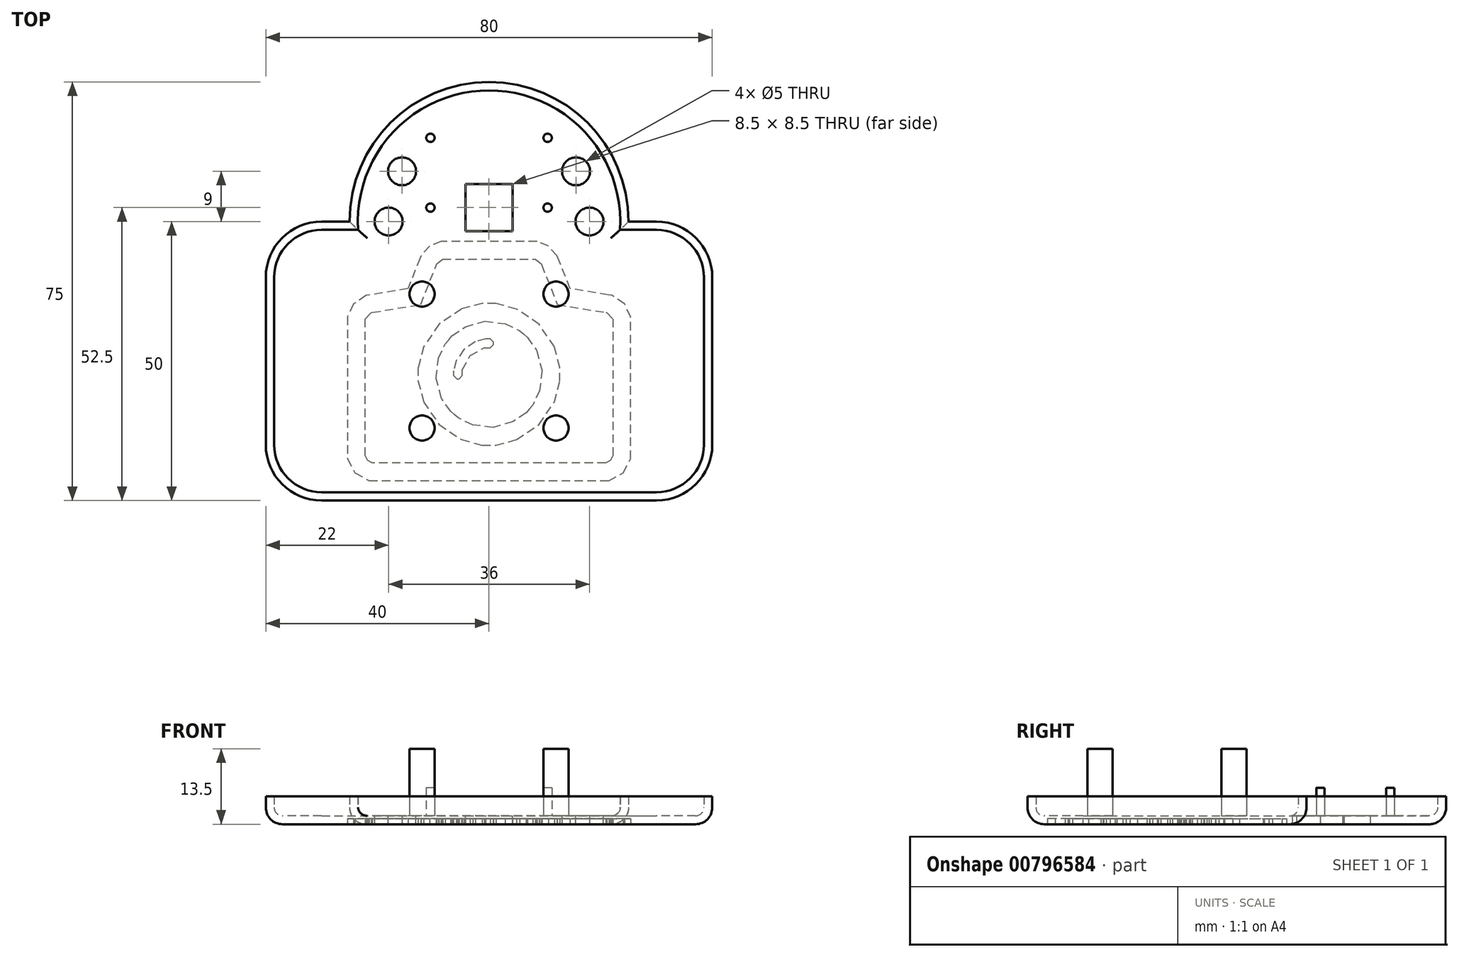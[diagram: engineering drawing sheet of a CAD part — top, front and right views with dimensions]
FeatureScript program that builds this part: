
annotation { "Feature Type Name" : "Feature", "Feature Type Description" : "" }
export const myFeature = defineFeature(function(context is Context, id is Id, definition is map)
    precondition{}
    {
        {
            var Q0;
            Q0=qCreatedBy(makeId("Top.planeOp"),FACE);
            var sketch = newSketch(context, id + "F0", { "sketchPlane" : qUnion([Q0])});
            skLineSegment(sketch, "E0.bottom", {"start": v(12.5, -12) * mm, "end": v(-12.5, -12) * mm});
            skLineSegment(sketch, "E0.top", {"start": v(12.5, 12) * mm, "end": v(-12.5, 12) * mm});
            skLineSegment(sketch, "E0.left", {"start": v(12.5, -12) * mm, "end": v(12.5, 12) * mm});
            skLineSegment(sketch, "E0.right", {"start": v(-12.5, -12) * mm, "end": v(-12.5, 12) * mm});
            skPoint(sketch, "E0.middle", {"position": v(0, 0) * mm});
            skPoint(sketch, "E1", {"position": v(-10.5, 10) * mm});
            skCircle(sketch, "E2", {"center": v(-10.5, 10) * mm, "radius": 0.75 * mm});
            skCircle(sketch, "E3.1.0.0", {"center": v(10.5, 10) * mm, "radius": 0.75 * mm});
            skLineSegment(sketch, "E3.direction1", {"start": v(-10.5, 10) * mm, "end": v(10.5, 10) * mm, "construction": true});
            skCircle(sketch, "E4.0.1.0", {"center": v(-10.5, -2.5) * mm, "radius": 0.75 * mm});
            skCircle(sketch, "E4.0.1.1", {"center": v(10.5, -2.5) * mm, "radius": 0.75 * mm});
            skLineSegment(sketch, "E4.direction1", {"start": v(-10.5, 10) * mm, "end": v(14.5, 10) * mm, "construction": true});
            skLineSegment(sketch, "E4.direction2", {"start": v(-10.5, 10) * mm, "end": v(-10.5, -2.5) * mm, "construction": true});
            skLineSegment(sketch, "E5.bottom", {"start": v(30, 25) * mm, "end": v(-30, 25) * mm});
            skLineSegment(sketch, "E5.top", {"start": v(30, -25) * mm, "end": v(-30, -25) * mm});
            skLineSegment(sketch, "E5.left", {"start": v(40, 15) * mm, "end": v(40, -15) * mm});
            skLineSegment(sketch, "E5.right", {"start": v(-40, 15) * mm, "end": v(-40, -15) * mm});
            skPoint(sketch, "E6.visualSharp", {"position": v(-40, 25) * mm});
            skArc(sketch, "E6.filletArc", {"start": v(-30, 25) * mm, "mid": v(-37.07, 22.07) * mm, "end": v(-40, 15) * mm});
            skPoint(sketch, "E7.visualSharp", {"position": v(40, 25) * mm});
            skArc(sketch, "E7.filletArc", {"start": v(40, 15) * mm, "mid": v(37.07, 22.07) * mm, "end": v(30, 25) * mm});
            skPoint(sketch, "E8.visualSharp", {"position": v(40, -25) * mm});
            skArc(sketch, "E8.filletArc", {"start": v(30, -25) * mm, "mid": v(37.07, -22.07) * mm, "end": v(40, -15) * mm});
            skPoint(sketch, "E9.visualSharp", {"position": v(-40, -25) * mm});
            skArc(sketch, "E9.filletArc", {"start": v(-40, -15) * mm, "mid": v(-37.07, -22.07) * mm, "end": v(-30, -25) * mm});
            skCircle(sketch, "E10", {"center": v(0, 25) * mm, "radius": 25 * mm});
            skSolve(sketch);
        }
        {
            var Q0;
            Q0=makeQuery(id+"F0.imprint","IMPRINT",FACE,{"disambiguationData":[TD([[makeQuery(id+"F0.imprint","IMPRINT",EDGE,{"derivedFrom":sQuery(id+"F0.wireOp",EDGE,"E0.bottom")}),1.0]])]});
            var Q1;
            Q1=makeQuery(id+"F0.imprint","IMPRINT",FACE,{"disambiguationData":[TD([[makeQuery(id+"F0.imprint","IMPRINT",EDGE,{"derivedFrom":sQuery(id+"F0.wireOp",EDGE,"E2")}),1.0]])]});
            var Q2;
            Q2=makeQuery(id+"F0.imprint","IMPRINT",FACE,{"disambiguationData":[TD([[makeQuery(id+"F0.imprint","IMPRINT",EDGE,{"derivedFrom":sQuery(id+"F0.wireOp",EDGE,"E3.1.0.0")}),1.0]])]});
            var Q3;
            Q3=makeQuery(id+"F0.imprint","IMPRINT",FACE,{"disambiguationData":[TD([[makeQuery(id+"F0.imprint","IMPRINT",EDGE,{"derivedFrom":sQuery(id+"F0.wireOp",EDGE,"E4.0.1.0")}),1.0]])]});
            var Q4;
            Q4=makeQuery(id+"F0.imprint","IMPRINT",FACE,{"disambiguationData":[TD([[makeQuery(id+"F0.imprint","IMPRINT",EDGE,{"derivedFrom":sQuery(id+"F0.wireOp",EDGE,"E4.0.1.1")}),1.0]])]});
            var Q5;
            Q5=makeQuery(id+"F0.imprint","IMPRINT",FACE,{"disambiguationData":[TD([[makeQuery(id+"F0.imprint","IMPRINT",EDGE,{"derivedFrom":sQuery(id+"F0.wireOp",EDGE,"E0.bottom")}),-1.0]])]});
            var Q6;
            {var subQ0=sQuery(id+"F0.wireOp",EDGE,"E10");var subQ1=sQuery(id+"F0.wireOp",EDGE,"E0.top");var subQ2=makeQuery(id+"F0.imprint","INTERSECT",VERTEX,{"disambiguationData":[OD(0.0)],"derivedFrom":[subQ1,subQ0]});Q6=makeQuery(id+"F0.imprint","IMPRINT",FACE,{"disambiguationData":[TD([[makeQuery(id+"F0.imprint","IMPRINT",EDGE,{"disambiguationData":[TD([[subQ2,-1.0]])],"derivedFrom":subQ1}),1.0]])]});}
            var Q7;
            {var subQ0=sQuery(id+"F0.wireOp",EDGE,"E10");var subQ1=sQuery(id+"F0.wireOp",EDGE,"E0.top");var subQ2=makeQuery(id+"F0.imprint","INTERSECT",VERTEX,{"disambiguationData":[OD(0.0)],"derivedFrom":[subQ1,subQ0]});Q7=makeQuery(id+"F0.imprint","IMPRINT",FACE,{"disambiguationData":[TD([[makeQuery(id+"F0.imprint","IMPRINT",EDGE,{"disambiguationData":[TD([[subQ2,-1.0]])],"derivedFrom":subQ1}),-1.0]])]});}
            var Q8;
            {var subQ0=sQuery(id+"F0.wireOp",EDGE,"E10");var subQ1=sQuery(id+"F0.wireOp",EDGE,"E5.bottom");var subQ2=makeQuery(id+"F0.imprint","INTERSECT",VERTEX,{"disambiguationData":[OD(0.0)],"derivedFrom":[subQ1,subQ0]});Q8=makeQuery(id+"F0.imprint","IMPRINT",FACE,{"disambiguationData":[TD([[makeQuery(id+"F0.imprint","IMPRINT",EDGE,{"disambiguationData":[TD([[subQ2,-1.0]])],"derivedFrom":subQ1}),-1.0]])]});}
            extrude(context, id + "F1", {"entities" : qUnion([Q0, Q1, Q2, Q3, Q4, Q5, Q6, Q7, Q8]), "depth" : 5 * mm, "offsetDistance" : 25 * mm});
        }
        {
            var Q0;
            Q0=makeQuery(id+"F1.opExtrude","CAP_EDGE",EDGE,{"disambiguationData":[OSD([sQuery(id+"F0.wireOp",EDGE,"E10")])],"isStart":true});
            var Q1;
            Q1=makeQuery(id+"F1.opExtrude","CAP_EDGE",EDGE,{"disambiguationData":[OSD([sQuery(id+"F0.wireOp",EDGE,"E5.right")])],"isStart":true});
            fillet(context, id + "F2", {"entities" : qUnion([Q0, Q1]), "radius" : 3 * mm, "tangentPropagation" : true, "allowEdgeOverflow" : false});
        }
        {
            var Q0;
            Q0=makeQuery(id+"F1.opExtrude","CAP_FACE",FACE,{"disambiguationData":[OSD([sQuery(id+"F0.wireOp",EDGE,"E5.bottom"),sQuery(id+"F0.wireOp",EDGE,"E5.top"),sQuery(id+"F0.wireOp",EDGE,"E5.left"),sQuery(id+"F0.wireOp",EDGE,"E5.right"),sQuery(id+"F0.wireOp",EDGE,"E6.filletArc"),sQuery(id+"F0.wireOp",EDGE,"E7.filletArc"),sQuery(id+"F0.wireOp",EDGE,"E8.filletArc"),sQuery(id+"F0.wireOp",EDGE,"E9.filletArc")])],"isStart":false});
            shell(context, id + "F3", {"entities" : qUnion([Q0]), "thickness" : 1.5 * mm});
        }
        {
            var Q0;
            Q0=makeQuery(id+"F3.opShell","OFFSET_FACE",FACE,{"disambiguationData":[OSD([sQuery(id+"F0.wireOp",EDGE,"E5.bottom"),sQuery(id+"F0.wireOp",EDGE,"E5.top"),sQuery(id+"F0.wireOp",EDGE,"E5.left"),sQuery(id+"F0.wireOp",EDGE,"E5.right"),sQuery(id+"F0.wireOp",EDGE,"E6.filletArc"),sQuery(id+"F0.wireOp",EDGE,"E7.filletArc"),sQuery(id+"F0.wireOp",EDGE,"E8.filletArc"),sQuery(id+"F0.wireOp",EDGE,"E9.filletArc")])]});
            var sketch = newSketch(context, id + "F4", { "sketchPlane" : qUnion([Q0])});
            skCircle(sketch, "E11", {"center": v(-12, 12) * mm, "radius": 2.25 * mm});
            skCircle(sketch, "E12.1.0", {"center": v(-12, -12) * mm, "radius": 2.25 * mm});
            skCircle(sketch, "E12.2.0", {"center": v(12, -12) * mm, "radius": 2.25 * mm});
            skCircle(sketch, "E12.3.0", {"center": v(12, 12) * mm, "radius": 2.25 * mm});
            skPoint(sketch, "E12.center", {"position": v(0, 0) * mm});
            skSolve(sketch);
        }
        {
            var Q0;
            Q0=makeQuery(id+"F4.imprint","IMPRINT",FACE,{"disambiguationData":[TD([[makeQuery(id+"F4.imprint","IMPRINT",EDGE,{"derivedFrom":sQuery(id+"F4.wireOp",EDGE,"E11")}),1.0]])]});
            var Q1;
            Q1=makeQuery(id+"F4.imprint","IMPRINT",FACE,{"disambiguationData":[TD([[makeQuery(id+"F4.imprint","IMPRINT",EDGE,{"derivedFrom":sQuery(id+"F4.wireOp",EDGE,"E12.3.0")}),1.0]])]});
            var Q2;
            Q2=makeQuery(id+"F4.imprint","IMPRINT",FACE,{"disambiguationData":[TD([[makeQuery(id+"F4.imprint","IMPRINT",EDGE,{"derivedFrom":sQuery(id+"F4.wireOp",EDGE,"E12.1.0")}),1.0]])]});
            var Q3;
            Q3=makeQuery(id+"F4.imprint","IMPRINT",FACE,{"disambiguationData":[TD([[makeQuery(id+"F4.imprint","IMPRINT",EDGE,{"derivedFrom":sQuery(id+"F4.wireOp",EDGE,"E12.2.0")}),1.0]])]});
            extrude(context, id + "F5", {"entities" : qUnion([Q0, Q1, Q2, Q3]), "operationType" : NewBodyOperationType.ADD, "depth" : 12 * mm, "offsetDistance" : 25 * mm});
        }
        {
            var Q0;
            Q0=makeQuery(id+"F3.opShell","OFFSET_FACE",FACE,{"disambiguationData":[OSD([sQuery(id+"F0.wireOp",EDGE,"E5.bottom"),sQuery(id+"F0.wireOp",EDGE,"E5.top"),sQuery(id+"F0.wireOp",EDGE,"E5.left"),sQuery(id+"F0.wireOp",EDGE,"E5.right"),sQuery(id+"F0.wireOp",EDGE,"E6.filletArc"),sQuery(id+"F0.wireOp",EDGE,"E7.filletArc"),sQuery(id+"F0.wireOp",EDGE,"E8.filletArc"),sQuery(id+"F0.wireOp",EDGE,"E9.filletArc"),sQuery(id+"F0.wireOp",EDGE,"E10")])]});
            var sketch = newSketch(context, id + "F6", { "sketchPlane" : qUnion([Q0])});
            skLineSegment(sketch, "E13.bottom", {"start": v(12.5, 18) * mm, "end": v(-12.5, 18) * mm});
            skLineSegment(sketch, "E13.top", {"start": v(12.5, 42) * mm, "end": v(-12.5, 42) * mm});
            skLineSegment(sketch, "E13.left", {"start": v(12.5, 18) * mm, "end": v(12.5, 42) * mm});
            skLineSegment(sketch, "E13.right", {"start": v(-12.5, 18) * mm, "end": v(-12.5, 42) * mm});
            skPoint(sketch, "E13.middle", {"position": v(0, 30) * mm});
            skPoint(sketch, "E14", {"position": v(-10.5, 40) * mm});
            skCircle(sketch, "E15", {"center": v(-10.5, 40) * mm, "radius": 0.75 * mm});
            skCircle(sketch, "E16.1.0.0", {"center": v(10.5, 40) * mm, "radius": 0.75 * mm});
            skLineSegment(sketch, "E16.direction1", {"start": v(-10.5, 40) * mm, "end": v(10.5, 40) * mm, "construction": true});
            skCircle(sketch, "E17.0.1.0", {"center": v(-10.5, 27.5) * mm, "radius": 0.75 * mm});
            skCircle(sketch, "E17.0.1.1", {"center": v(10.5, 27.5) * mm, "radius": 0.75 * mm});
            skLineSegment(sketch, "E17.direction1", {"start": v(-10.5, 40) * mm, "end": v(14.5, 40) * mm, "construction": true});
            skLineSegment(sketch, "E17.direction2", {"start": v(-10.5, 40) * mm, "end": v(-10.5, 27.5) * mm, "construction": true});
            skLineSegment(sketch, "E18.bottom", {"start": v(-4.25, 31.75) * mm, "end": v(4.25, 31.75) * mm});
            skLineSegment(sketch, "E18.top", {"start": v(-4.25, 23.25) * mm, "end": v(4.25, 23.25) * mm});
            skLineSegment(sketch, "E18.left", {"start": v(-4.25, 31.75) * mm, "end": v(-4.25, 23.25) * mm});
            skLineSegment(sketch, "E18.right", {"start": v(4.25, 31.75) * mm, "end": v(4.25, 23.25) * mm});
            skSolve(sketch);
        }
        {
            var Q0;
            Q0=makeQuery(id+"F6.imprint","IMPRINT",FACE,{"disambiguationData":[TD([[makeQuery(id+"F6.imprint","IMPRINT",EDGE,{"derivedFrom":sQuery(id+"F6.wireOp",EDGE,"E15")}),1.0]])]});
            var Q1;
            Q1=makeQuery(id+"F6.imprint","IMPRINT",FACE,{"disambiguationData":[TD([[makeQuery(id+"F6.imprint","IMPRINT",EDGE,{"derivedFrom":sQuery(id+"F6.wireOp",EDGE,"E16.1.0.0")}),1.0]])]});
            var Q2;
            Q2=makeQuery(id+"F6.imprint","IMPRINT",FACE,{"disambiguationData":[TD([[makeQuery(id+"F6.imprint","IMPRINT",EDGE,{"derivedFrom":sQuery(id+"F6.wireOp",EDGE,"E17.0.1.0")}),1.0]])]});
            var Q3;
            Q3=makeQuery(id+"F6.imprint","IMPRINT",FACE,{"disambiguationData":[TD([[makeQuery(id+"F6.imprint","IMPRINT",EDGE,{"derivedFrom":sQuery(id+"F6.wireOp",EDGE,"E17.0.1.1")}),1.0]])]});
            extrude(context, id + "F7", {"entities" : qUnion([Q0, Q1, Q2, Q3]), "operationType" : NewBodyOperationType.ADD, "depth" : 5 * mm, "offsetDistance" : 25 * mm});
        }
        {
            var Q0;
            Q0=makeQuery(id+"F6.imprint","IMPRINT",FACE,{"disambiguationData":[TD([[makeQuery(id+"F6.imprint","IMPRINT",EDGE,{"derivedFrom":sQuery(id+"F6.wireOp",EDGE,"E18.bottom")}),-1.0]])]});
            extrude(context, id + "F8", {"entities" : qUnion([Q0]), "operationType" : NewBodyOperationType.REMOVE, "oppositeDirection" : true, "depth" : 25 * mm, "offsetDistance" : 25 * mm});
        }
        {
            var Q0;
            Q0=makeQuery(id+"F6.imprint","IMPRINT",FACE,{"disambiguationData":[TD([[makeQuery(id+"F6.imprint","IMPRINT",EDGE,{"derivedFrom":sQuery(id+"F6.wireOp",EDGE,"E13.bottom")}),1.0]])]});
            var sketch = newSketch(context, id + "F9", { "sketchPlane" : qUnion([Q0])});
            skPoint(sketch, "E19", {"position": v(0, 43) * mm});
            skPoint(sketch, "E20", {"position": v(0, 25) * mm});
            skPoint(sketch, "E21.1.0", {"position": v(-9, 40.59) * mm});
            skPoint(sketch, "E21.2.0", {"position": v(-15.59, 34) * mm});
            skPoint(sketch, "E21.3.0", {"position": v(-18, 25) * mm});
            skPoint(sketch, "E21.4.0", {"position": v(-15.59, 16) * mm});
            skPoint(sketch, "E21.5.0", {"position": v(-9, 9.41) * mm});
            skPoint(sketch, "E21.6.0", {"position": v(0, 7) * mm});
            skPoint(sketch, "E21.7.0", {"position": v(9, 9.41) * mm});
            skPoint(sketch, "E21.8.0", {"position": v(15.59, 16) * mm});
            skPoint(sketch, "E21.9.0", {"position": v(18, 25) * mm});
            skPoint(sketch, "E21.10.0", {"position": v(15.59, 34) * mm});
            skPoint(sketch, "E21.11.0", {"position": v(9, 40.59) * mm});
            skSolve(sketch);
        }
        {
            var Q0;
            Q0=sQuery(id+"F9.wireOp",VERTEX,"E21.2.0");
            var Q1;
            Q1=sQuery(id+"F9.wireOp",VERTEX,"E21.3.0");
            var Q2;
            Q2=sQuery(id+"F9.wireOp",VERTEX,"E21.10.0");
            var Q3;
            Q3=sQuery(id+"F9.wireOp",VERTEX,"E21.9.0");
            var Q4;
            Q4=makeQuery(id+"F1.opExtrude","SWEPT_BODY",BODY,{"disambiguationData":[OSD([sQuery(id+"F0.wireOp",EDGE,"E5.bottom"),sQuery(id+"F0.wireOp",EDGE,"E5.top"),sQuery(id+"F0.wireOp",EDGE,"E5.left"),sQuery(id+"F0.wireOp",EDGE,"E5.right"),sQuery(id+"F0.wireOp",EDGE,"E6.filletArc"),sQuery(id+"F0.wireOp",EDGE,"E7.filletArc"),sQuery(id+"F0.wireOp",EDGE,"E8.filletArc"),sQuery(id+"F0.wireOp",EDGE,"E9.filletArc"),sQuery(id+"F0.wireOp",EDGE,"E10")])]});
            hole(context, id + "F10", {"style" : HoleStyle.SIMPLE, "endStyle" : HoleEndStyle.THROUGH, "holeDiameter" : 5 * mm, "majorDiameter" : 5 * mm, "isTappedThrough" : true, "tappedDepth" : 12 * mm, "tapClearance" : 3, "locations" : qUnion([Q0, Q1, Q2, Q3]), "scope" : qUnion([Q4])});
        }
        {
            var Q0;
            Q0=qCreatedBy(makeId("Top.planeOp"),FACE);
            var sketch = newSketch(context, id + "F11", { "sketchPlane" : qUnion([Q0])});
            skLineSegment(sketch, "E22", {"start": v(0, 20.64) * mm, "end": v(-2.48, 20.64) * mm});
            skLineSegment(sketch, "E23", {"start": v(-2.48, 20.64) * mm, "end": v(-9.89, 18.65) * mm});
            skLineSegment(sketch, "E24", {"start": v(-9.89, 18.65) * mm, "end": v(-17.96, 13.2) * mm});
            skLineSegment(sketch, "E25", {"start": v(-17.96, 13.2) * mm, "end": v(-23.42, 5.13) * mm});
            skLineSegment(sketch, "E26", {"start": v(-23.42, 5.13) * mm, "end": v(-25.4, -2.28) * mm});
            skLineSegment(sketch, "E27", {"start": v(-25.4, -2.28) * mm, "end": v(-25.4, -4.76) * mm});
            skLineSegment(sketch, "E28", {"start": v(-25.4, -4.76) * mm, "end": v(-25.4, -7.23) * mm});
            skLineSegment(sketch, "E29", {"start": v(-25.4, -7.23) * mm, "end": v(-23.42, -14.63) * mm});
            skLineSegment(sketch, "E30", {"start": v(-23.42, -14.63) * mm, "end": v(-17.96, -22.72) * mm});
            skLineSegment(sketch, "E31", {"start": v(-17.96, -22.72) * mm, "end": v(-9.89, -28.16) * mm});
            skLineSegment(sketch, "E32", {"start": v(-9.89, -28.16) * mm, "end": v(-2.48, -30.16) * mm});
            skLineSegment(sketch, "E33", {"start": v(-2.48, -30.16) * mm, "end": v(0, -30.16) * mm});
            skLineSegment(sketch, "E34", {"start": v(0, -30.16) * mm, "end": v(2.46, -30.16) * mm});
            skLineSegment(sketch, "E35", {"start": v(2.46, -30.16) * mm, "end": v(9.87, -28.16) * mm});
            skLineSegment(sketch, "E36", {"start": v(9.87, -28.16) * mm, "end": v(17.96, -22.72) * mm});
            skLineSegment(sketch, "E37", {"start": v(17.96, -22.72) * mm, "end": v(23.4, -14.63) * mm});
            skLineSegment(sketch, "E38", {"start": v(23.4, -14.63) * mm, "end": v(25.4, -7.23) * mm});
            skLineSegment(sketch, "E39", {"start": v(25.4, -7.23) * mm, "end": v(25.4, -4.76) * mm});
            skLineSegment(sketch, "E40", {"start": v(25.4, -4.76) * mm, "end": v(25.4, -2.28) * mm});
            skLineSegment(sketch, "E41", {"start": v(25.4, -2.28) * mm, "end": v(23.4, 5.13) * mm});
            skLineSegment(sketch, "E42", {"start": v(23.4, 5.13) * mm, "end": v(17.96, 13.2) * mm});
            skLineSegment(sketch, "E43", {"start": v(17.96, 13.2) * mm, "end": v(9.87, 18.65) * mm});
            skLineSegment(sketch, "E44", {"start": v(9.87, 18.65) * mm, "end": v(2.46, 20.64) * mm});
            skLineSegment(sketch, "E45", {"start": v(2.46, 20.64) * mm, "end": v(0, 20.64) * mm});
            skLineSegment(sketch, "E46", {"start": v(14.47, -17.16) * mm, "end": v(13.26, -18.57) * mm});
            skLineSegment(sketch, "E47", {"start": v(13.26, -18.57) * mm, "end": v(8.5, -21.81) * mm});
            skLineSegment(sketch, "E48", {"start": v(8.5, -21.81) * mm, "end": v(1.46, -23.75) * mm});
            skLineSegment(sketch, "E49", {"start": v(1.46, -23.75) * mm, "end": v(-5.8, -22.92) * mm});
            skLineSegment(sketch, "E50", {"start": v(-5.8, -22.92) * mm, "end": v(-11, -20.42) * mm});
            skLineSegment(sketch, "E51", {"start": v(-11, -20.42) * mm, "end": v(-12.4, -19.23) * mm});
            skLineSegment(sketch, "E52", {"start": v(-12.4, -19.23) * mm, "end": v(-13.8, -18.02) * mm});
            skLineSegment(sketch, "E53", {"start": v(-13.8, -18.02) * mm, "end": v(-17.07, -13.26) * mm});
            skLineSegment(sketch, "E54", {"start": v(-17.07, -13.26) * mm, "end": v(-19, -6.22) * mm});
            skLineSegment(sketch, "E55", {"start": v(-19, -6.22) * mm, "end": v(-18.16, 1.03) * mm});
            skLineSegment(sketch, "E56", {"start": v(-18.16, 1.03) * mm, "end": v(-15.66, 6.22) * mm});
            skLineSegment(sketch, "E57", {"start": v(-15.66, 6.22) * mm, "end": v(-14.45, 7.62) * mm});
            skLineSegment(sketch, "E58", {"start": v(-14.45, 7.62) * mm, "end": v(-13.26, 9.03) * mm});
            skLineSegment(sketch, "E59", {"start": v(-13.26, 9.03) * mm, "end": v(-8.5, 12.29) * mm});
            skLineSegment(sketch, "E60", {"start": v(-8.5, 12.29) * mm, "end": v(-1.47, 14.24) * mm});
            skLineSegment(sketch, "E61", {"start": v(-1.47, 14.24) * mm, "end": v(5.79, 13.4) * mm});
            skLineSegment(sketch, "E62", {"start": v(5.79, 13.4) * mm, "end": v(10.98, 10.9) * mm});
            skLineSegment(sketch, "E63", {"start": v(10.98, 10.9) * mm, "end": v(12.4, 9.7) * mm});
            skLineSegment(sketch, "E64", {"start": v(12.4, 9.7) * mm, "end": v(13.8, 8.5) * mm});
            skLineSegment(sketch, "E65", {"start": v(13.8, 8.5) * mm, "end": v(17.05, 3.74) * mm});
            skLineSegment(sketch, "E66", {"start": v(17.05, 3.74) * mm, "end": v(18.98, -3.3) * mm});
            skLineSegment(sketch, "E67", {"start": v(18.98, -3.3) * mm, "end": v(18.16, -10.55) * mm});
            skLineSegment(sketch, "E68", {"start": v(18.16, -10.55) * mm, "end": v(15.68, -15.76) * mm});
            skLineSegment(sketch, "E69", {"start": v(15.68, -15.76) * mm, "end": v(14.47, -17.16) * mm});
            skLineSegment(sketch, "E70", {"start": v(0, 7.94) * mm, "end": v(-1.24, 7.94) * mm});
            skLineSegment(sketch, "E71", {"start": v(-1.24, 7.94) * mm, "end": v(-4.94, 6.95) * mm});
            skLineSegment(sketch, "E72", {"start": v(-4.94, 6.95) * mm, "end": v(-8.98, 4.22) * mm});
            skLineSegment(sketch, "E73", {"start": v(-8.98, 4.22) * mm, "end": v(-11.7, 0.18) * mm});
            skLineSegment(sketch, "E74", {"start": v(-11.7, 0.18) * mm, "end": v(-12.7, -3.52) * mm});
            skLineSegment(sketch, "E75", {"start": v(-12.7, -3.52) * mm, "end": v(-12.7, -4.76) * mm});
            skLineSegment(sketch, "E76", {"start": v(-12.7, -4.76) * mm, "end": v(-12.7, -5.16) * mm});
            skLineSegment(sketch, "E77", {"start": v(-12.7, -5.16) * mm, "end": v(-11.5, -6.35) * mm});
            skLineSegment(sketch, "E78", {"start": v(-11.5, -6.35) * mm, "end": v(-11.11, -6.35) * mm});
            skLineSegment(sketch, "E79", {"start": v(-11.11, -6.35) * mm, "end": v(-10.72, -6.35) * mm});
            skLineSegment(sketch, "E80", {"start": v(-10.72, -6.35) * mm, "end": v(-9.52, -5.16) * mm});
            skLineSegment(sketch, "E81", {"start": v(-9.52, -5.16) * mm, "end": v(-9.52, -4.76) * mm});
            skLineSegment(sketch, "E82", {"start": v(-9.52, -4.76) * mm, "end": v(-9.52, -3.08) * mm});
            skLineSegment(sketch, "E83", {"start": v(-9.52, -3.08) * mm, "end": v(-6.75, 1.98) * mm});
            skLineSegment(sketch, "E84", {"start": v(-6.75, 1.98) * mm, "end": v(-1.69, 4.76) * mm});
            skLineSegment(sketch, "E85", {"start": v(-1.69, 4.76) * mm, "end": v(0, 4.76) * mm});
            skLineSegment(sketch, "E86", {"start": v(0, 4.76) * mm, "end": v(0.4, 4.76) * mm});
            skLineSegment(sketch, "E87", {"start": v(0.4, 4.76) * mm, "end": v(1.59, 5.95) * mm});
            skLineSegment(sketch, "E88", {"start": v(1.59, 5.95) * mm, "end": v(1.59, 6.35) * mm});
            skLineSegment(sketch, "E89", {"start": v(1.59, 6.35) * mm, "end": v(1.59, 6.75) * mm});
            skLineSegment(sketch, "E90", {"start": v(1.59, 6.75) * mm, "end": v(0.4, 7.94) * mm});
            skLineSegment(sketch, "E91", {"start": v(0.4, 7.94) * mm, "end": v(0, 7.94) * mm});
            skLineSegment(sketch, "E92", {"start": v(42.83, 23.68) * mm, "end": v(29.07, 25.98) * mm});
            skLineSegment(sketch, "E93", {"start": v(29.07, 25.98) * mm, "end": v(24.72, 36.88) * mm});
            skLineSegment(sketch, "E94", {"start": v(24.72, 36.88) * mm, "end": v(24.36, 37.79) * mm});
            skLineSegment(sketch, "E95", {"start": v(24.36, 37.79) * mm, "end": v(21.22, 41.24) * mm});
            skLineSegment(sketch, "E96", {"start": v(21.22, 41.24) * mm, "end": v(17.2, 42.86) * mm});
            skLineSegment(sketch, "E97", {"start": v(17.2, 42.86) * mm, "end": v(15.88, 42.86) * mm});
            skLineSegment(sketch, "E98", {"start": v(15.88, 42.86) * mm, "end": v(-15.87, 42.86) * mm});
            skLineSegment(sketch, "E99", {"start": v(-15.87, 42.86) * mm, "end": v(-17.21, 42.86) * mm});
            skLineSegment(sketch, "E100", {"start": v(-17.21, 42.86) * mm, "end": v(-21.23, 41.24) * mm});
            skLineSegment(sketch, "E101", {"start": v(-21.23, 41.24) * mm, "end": v(-24.36, 37.79) * mm});
            skLineSegment(sketch, "E102", {"start": v(-24.36, 37.79) * mm, "end": v(-24.72, 36.88) * mm});
            skLineSegment(sketch, "E103", {"start": v(-24.72, 36.88) * mm, "end": v(-29.07, 25.98) * mm});
            skLineSegment(sketch, "E104", {"start": v(-29.07, 25.98) * mm, "end": v(-42.83, 23.68) * mm});
            skLineSegment(sketch, "E105", {"start": v(-42.83, 23.68) * mm, "end": v(-43.99, 23.5) * mm});
            skLineSegment(sketch, "E106", {"start": v(-43.99, 23.5) * mm, "end": v(-48.55, 20.46) * mm});
            skLineSegment(sketch, "E107", {"start": v(-48.55, 20.46) * mm, "end": v(-50.8, 15.84) * mm});
            skLineSegment(sketch, "E108", {"start": v(-50.8, 15.84) * mm, "end": v(-50.8, 14.29) * mm});
            skLineSegment(sketch, "E109", {"start": v(-50.8, 14.29) * mm, "end": v(-50.8, -33.34) * mm});
            skLineSegment(sketch, "E110", {"start": v(-50.8, -33.34) * mm, "end": v(-50.8, -35) * mm});
            skLineSegment(sketch, "E111", {"start": v(-50.8, -35) * mm, "end": v(-48.02, -40.07) * mm});
            skLineSegment(sketch, "E112", {"start": v(-48.02, -40.07) * mm, "end": v(-42.96, -42.86) * mm});
            skLineSegment(sketch, "E113", {"start": v(-42.96, -42.86) * mm, "end": v(-41.27, -42.86) * mm});
            skLineSegment(sketch, "E114", {"start": v(-41.27, -42.86) * mm, "end": v(41.28, -42.86) * mm});
            skLineSegment(sketch, "E115", {"start": v(41.28, -42.86) * mm, "end": v(42.95, -42.86) * mm});
            skLineSegment(sketch, "E116", {"start": v(42.95, -42.86) * mm, "end": v(48, -40.07) * mm});
            skLineSegment(sketch, "E117", {"start": v(48, -40.07) * mm, "end": v(50.8, -35) * mm});
            skLineSegment(sketch, "E118", {"start": v(50.8, -35) * mm, "end": v(50.8, -33.34) * mm});
            skLineSegment(sketch, "E119", {"start": v(50.8, -33.34) * mm, "end": v(50.8, 14.29) * mm});
            skLineSegment(sketch, "E120", {"start": v(50.8, 14.29) * mm, "end": v(50.8, 15.84) * mm});
            skLineSegment(sketch, "E121", {"start": v(50.8, 15.84) * mm, "end": v(48.53, 20.46) * mm});
            skLineSegment(sketch, "E122", {"start": v(48.53, 20.46) * mm, "end": v(43.97, 23.5) * mm});
            skLineSegment(sketch, "E123", {"start": v(43.97, 23.5) * mm, "end": v(42.83, 23.68) * mm});
            skLineSegment(sketch, "E124", {"start": v(44.45, -33.34) * mm, "end": v(44.45, -33.88) * mm});
            skLineSegment(sketch, "E125", {"start": v(44.45, -33.88) * mm, "end": v(43.5, -35.57) * mm});
            skLineSegment(sketch, "E126", {"start": v(43.5, -35.57) * mm, "end": v(41.82, -36.51) * mm});
            skLineSegment(sketch, "E127", {"start": v(41.82, -36.51) * mm, "end": v(41.28, -36.51) * mm});
            skLineSegment(sketch, "E128", {"start": v(41.28, -36.51) * mm, "end": v(-41.27, -36.51) * mm});
            skLineSegment(sketch, "E129", {"start": v(-41.27, -36.51) * mm, "end": v(-41.84, -36.51) * mm});
            skLineSegment(sketch, "E130", {"start": v(-41.84, -36.51) * mm, "end": v(-43.52, -35.57) * mm});
            skLineSegment(sketch, "E131", {"start": v(-43.52, -35.57) * mm, "end": v(-44.45, -33.88) * mm});
            skLineSegment(sketch, "E132", {"start": v(-44.45, -33.88) * mm, "end": v(-44.45, -33.34) * mm});
            skLineSegment(sketch, "E133", {"start": v(-44.45, -33.34) * mm, "end": v(-44.45, 14.29) * mm});
            skLineSegment(sketch, "E134", {"start": v(-44.45, 14.29) * mm, "end": v(-44.45, 15.08) * mm});
            skLineSegment(sketch, "E135", {"start": v(-44.45, 15.08) * mm, "end": v(-42.18, 17.36) * mm});
            skLineSegment(sketch, "E136", {"start": v(-42.18, 17.36) * mm, "end": v(-41.79, 17.41) * mm});
            skLineSegment(sketch, "E137", {"start": v(-41.79, 17.41) * mm, "end": v(-24.5, 20.3) * mm});
            skLineSegment(sketch, "E138", {"start": v(-24.5, 20.3) * mm, "end": v(-18.82, 34.51) * mm});
            skLineSegment(sketch, "E139", {"start": v(-18.82, 34.51) * mm, "end": v(-18.7, 34.83) * mm});
            skLineSegment(sketch, "E140", {"start": v(-18.7, 34.83) * mm, "end": v(-16.59, 36.51) * mm});
            skLineSegment(sketch, "E141", {"start": v(-16.59, 36.51) * mm, "end": v(-15.87, 36.51) * mm});
            skLineSegment(sketch, "E142", {"start": v(-15.87, 36.51) * mm, "end": v(15.88, 36.51) * mm});
            skLineSegment(sketch, "E143", {"start": v(15.88, 36.51) * mm, "end": v(16.6, 36.51) * mm});
            skLineSegment(sketch, "E144", {"start": v(16.6, 36.51) * mm, "end": v(18.69, 34.83) * mm});
            skLineSegment(sketch, "E145", {"start": v(18.69, 34.83) * mm, "end": v(18.82, 34.51) * mm});
            skLineSegment(sketch, "E146", {"start": v(18.82, 34.51) * mm, "end": v(24.5, 20.3) * mm});
            skLineSegment(sketch, "E147", {"start": v(24.5, 20.3) * mm, "end": v(41.79, 17.41) * mm});
            skLineSegment(sketch, "E148", {"start": v(41.79, 17.41) * mm, "end": v(42.17, 17.36) * mm});
            skLineSegment(sketch, "E149", {"start": v(42.17, 17.36) * mm, "end": v(44.45, 15.06) * mm});
            skLineSegment(sketch, "E150", {"start": v(44.45, 15.06) * mm, "end": v(44.45, 14.29) * mm});
            skLineSegment(sketch, "E151", {"start": v(44.45, 14.29) * mm, "end": v(44.45, -33.34) * mm});
            skSolve(sketch);
        }
        {
            var Q0;
            Q0=makeQuery(id+"F1.opExtrude","SWEPT_BODY",BODY,{"disambiguationData":[OSD([sQuery(id+"F0.wireOp",EDGE,"E5.bottom"),sQuery(id+"F0.wireOp",EDGE,"E5.top"),sQuery(id+"F0.wireOp",EDGE,"E5.left"),sQuery(id+"F0.wireOp",EDGE,"E5.right"),sQuery(id+"F0.wireOp",EDGE,"E6.filletArc"),sQuery(id+"F0.wireOp",EDGE,"E7.filletArc"),sQuery(id+"F0.wireOp",EDGE,"E8.filletArc"),sQuery(id+"F0.wireOp",EDGE,"E9.filletArc"),sQuery(id+"F0.wireOp",EDGE,"E10")])]});
            var Q1;
            Q1=qCreatedBy(makeId("Origin.pointOp"),VERTEX);
            transform(context, id + "F12", {"entities" : qUnion([Q0]), "transformType" : TransformType.SCALE_UNIFORMLY, "scale" : 2, "scalePoint" : qUnion([Q1]), "makeCopy" : false});
        }
        {
            var Q0;
            Q0=makeQuery(id+"F11.imprint","IMPRINT",FACE,{"disambiguationData":[TD([[makeQuery(id+"F11.imprint","IMPRINT",EDGE,{"derivedFrom":sQuery(id+"F11.wireOp",EDGE,"E92")}),1.0]])]});
            var Q1;
            Q1=makeQuery(id+"F11.imprint","IMPRINT",FACE,{"disambiguationData":[TD([[makeQuery(id+"F11.imprint","IMPRINT",EDGE,{"derivedFrom":sQuery(id+"F11.wireOp",EDGE,"E22")}),1.0]])]});
            var Q2;
            Q2=makeQuery(id+"F11.imprint","IMPRINT",FACE,{"disambiguationData":[TD([[makeQuery(id+"F11.imprint","IMPRINT",EDGE,{"derivedFrom":sQuery(id+"F11.wireOp",EDGE,"E70")}),1.0]])]});
            extrude(context, id + "F13", {"entities" : qUnion([Q0, Q1, Q2]), "operationType" : NewBodyOperationType.REMOVE, "depth" : 2 * mm, "offsetDistance" : 25 * mm});
        }
        {
            var Q0;
            Q0=makeQuery(id+"F1.opExtrude","SWEPT_BODY",BODY,{"disambiguationData":[OSD([sQuery(id+"F0.wireOp",EDGE,"E5.bottom"),sQuery(id+"F0.wireOp",EDGE,"E5.top"),sQuery(id+"F0.wireOp",EDGE,"E5.left"),sQuery(id+"F0.wireOp",EDGE,"E5.right"),sQuery(id+"F0.wireOp",EDGE,"E6.filletArc"),sQuery(id+"F0.wireOp",EDGE,"E7.filletArc"),sQuery(id+"F0.wireOp",EDGE,"E8.filletArc"),sQuery(id+"F0.wireOp",EDGE,"E9.filletArc"),sQuery(id+"F0.wireOp",EDGE,"E10")])]});
            var Q1;
            Q1=qCreatedBy(makeId("Origin.pointOp"),VERTEX);
            var Q2;
            Q2=qCreatedBy(makeId("Origin.pointOp"),VERTEX);
            transform(context, id + "F14", {"entities" : qUnion([Q0]), "transformType" : TransformType.SCALE_UNIFORMLY, "scale" : .5, "scalePoint" : qUnion([Q2]), "makeCopy" : false});
        }
    });
